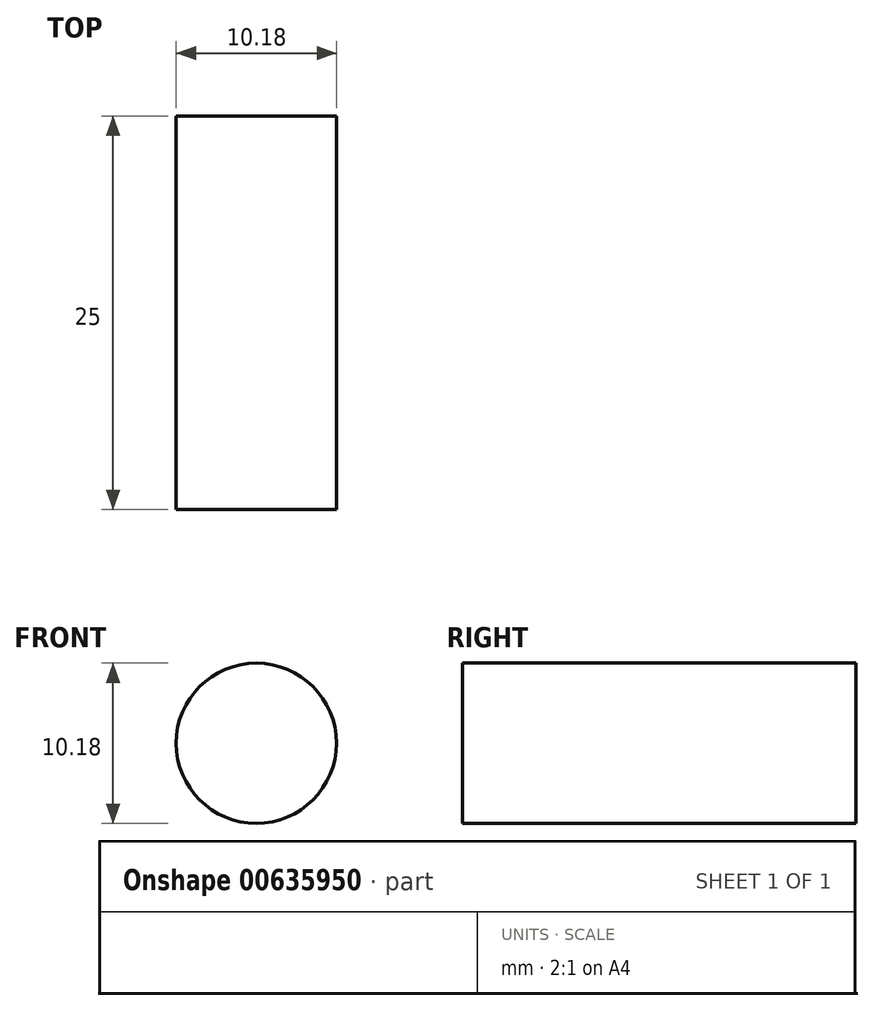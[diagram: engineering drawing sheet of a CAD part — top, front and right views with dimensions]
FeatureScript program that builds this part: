
annotation { "Feature Type Name" : "Feature", "Feature Type Description" : "" }
export const myFeature = defineFeature(function(context is Context, id is Id, definition is map)
    precondition{}
    {
        {
            var Q0;
            Q0=qCreatedBy(makeId("Front.planeOp"),FACE);
            var sketch = newSketch(context, id + "F0", { "sketchPlane" : qUnion([Q0])});
            skCircle(sketch, "E0", {"center": v(0, 0) * mm, "radius": 5.09 * mm});
            skSolve(sketch);
        }
        {
            var Q0;
            Q0=sQuery(id+"F0.wireOp",EDGE,"E0");
            extrude(context, id + "F1", {"bodyType" : ToolBodyType.SURFACE, "surfaceEntities" : qUnion([Q0]), "depth" : 25 * mm, "offsetDistance" : 25 * mm});
        }
    });
